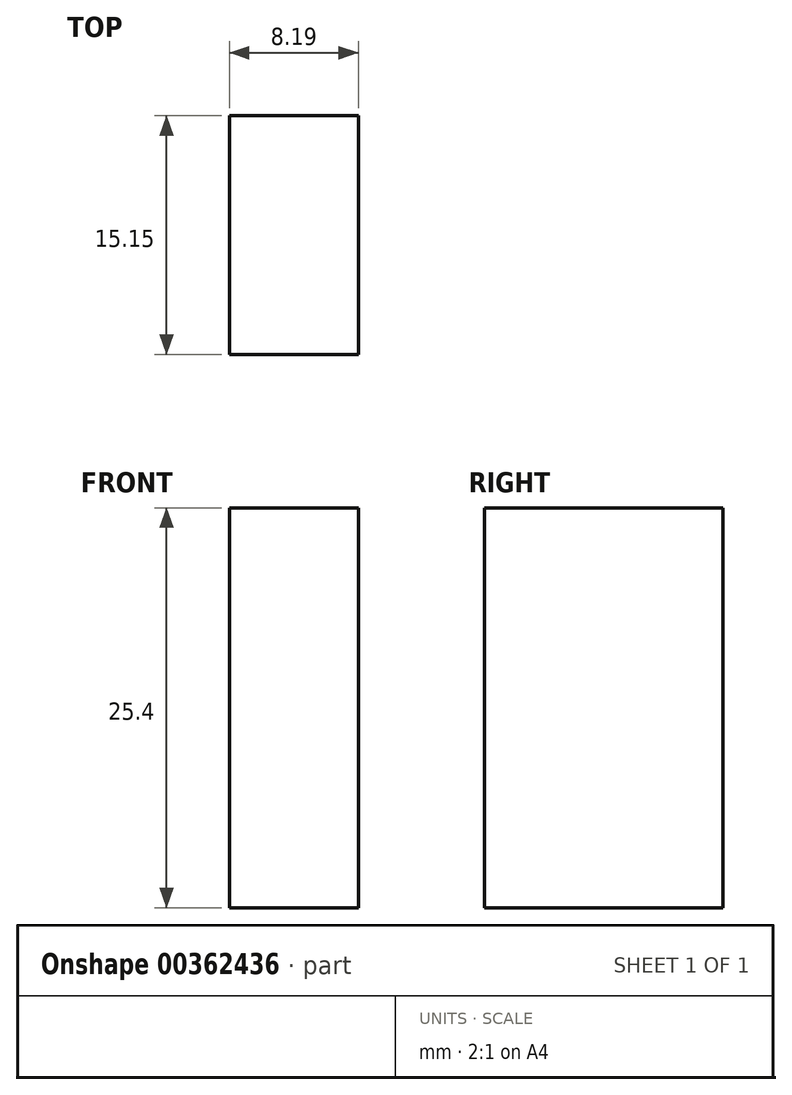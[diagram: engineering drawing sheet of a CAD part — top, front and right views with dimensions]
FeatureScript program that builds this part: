
annotation { "Feature Type Name" : "Feature", "Feature Type Description" : "" }
export const myFeature = defineFeature(function(context is Context, id is Id, definition is map)
    precondition{}
    {
        {
            var Q0;
            Q0=qCreatedBy(makeId("Top.planeOp"),FACE);
            var sketch = newSketch(context, id + "F0", { "sketchPlane" : qUnion([Q0])});
            skLineSegment(sketch, "E0.bottom", {"start": v(-34.83, 44) * mm, "end": v(-26.64, 44) * mm});
            skLineSegment(sketch, "E0.top", {"start": v(-34.83, 28.84) * mm, "end": v(-26.64, 28.84) * mm});
            skLineSegment(sketch, "E0.left", {"start": v(-34.83, 44) * mm, "end": v(-34.83, 28.84) * mm});
            skLineSegment(sketch, "E0.right", {"start": v(-26.64, 44) * mm, "end": v(-26.64, 28.84) * mm});
            skLineSegment(sketch, "E1.bottom", {"start": v(14.18, 28.84) * mm, "end": v(-26.64, 28.84) * mm});
            skLineSegment(sketch, "E1.top", {"start": v(14.18, 28.84) * mm, "end": v(-26.64, 28.84) * mm});
            skLineSegment(sketch, "E1.left", {"start": v(14.18, 28.84) * mm, "end": v(14.18, 28.84) * mm});
            skLineSegment(sketch, "E1.right", {"start": v(-26.64, 28.84) * mm, "end": v(-26.64, 28.84) * mm});
            skSolve(sketch);
        }
        {
            var Q0;
            Q0=makeQuery(id+"F0.imprint","IMPRINT",FACE,{"disambiguationData":[TD([[makeQuery(id+"F0.imprint","IMPRINT",EDGE,{"derivedFrom":sQuery(id+"F0.wireOp",EDGE,"E0.bottom")}),-1.0]])]});
            extrude(context, id + "F1", {"entities" : qUnion([Q0]), "depth" : 25.4 * mm});
        }
    });
